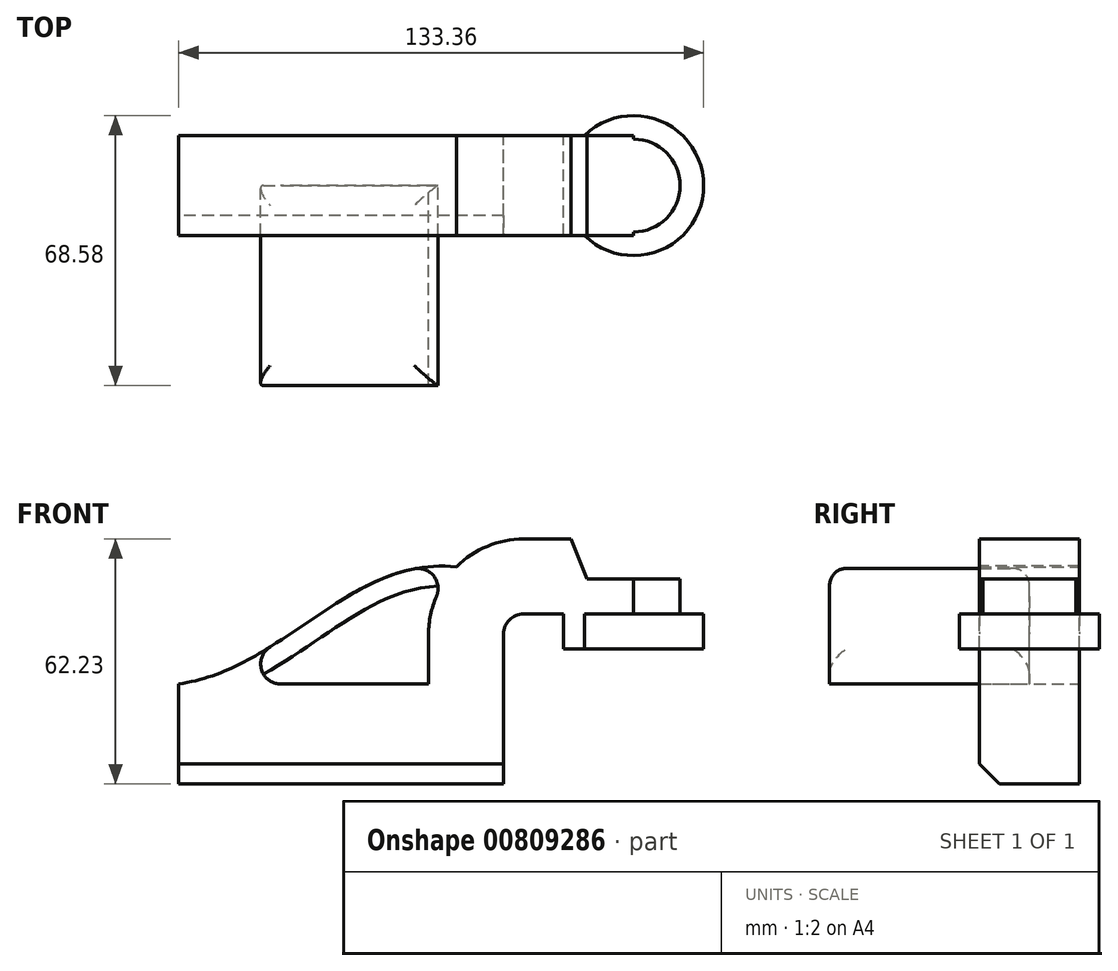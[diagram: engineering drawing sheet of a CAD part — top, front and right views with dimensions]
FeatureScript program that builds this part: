
annotation { "Feature Type Name" : "Feature", "Feature Type Description" : "" }
export const myFeature = defineFeature(function(context is Context, id is Id, definition is map)
    precondition{}
    {
        {
            var Q0;
            Q0=qCreatedBy(makeId("Front.planeOp"),FACE);
            var sketch = newSketch(context, id + "F0", { "sketchPlane" : qUnion([Q0])});
            skLineSegment(sketch, "E0.bottom", {"start": v(41.28, -12.7) * mm, "end": v(-41.28, -12.7) * mm});
            skLineSegment(sketch, "E0.top", {"start": v(41.28, 12.7) * mm, "end": v(-41.28, 12.7) * mm});
            skLineSegment(sketch, "E0.left", {"start": v(41.28, -12.7) * mm, "end": v(41.28, 12.7) * mm});
            skLineSegment(sketch, "E0.right", {"start": v(-41.28, -12.7) * mm, "end": v(-41.28, 12.7) * mm});
            skPoint(sketch, "E0.middle", {"position": v(0, 0) * mm});
            skLineSegment(sketch, "E1.bottom", {"start": v(74.3, 21.6) * mm, "end": v(56.52, 21.6) * mm});
            skLineSegment(sketch, "E1.top", {"start": v(74.3, 39.37) * mm, "end": v(56.52, 39.37) * mm});
            skLineSegment(sketch, "E1.left", {"start": v(74.3, 21.6) * mm, "end": v(74.3, 39.37) * mm});
            skLineSegment(sketch, "E1.right", {"start": v(56.52, 21.6) * mm, "end": v(56.52, 39.37) * mm});
            skPoint(sketch, "E1.middle", {"position": v(65.4, 30.48) * mm});
            skLineSegment(sketch, "E2", {"start": v(41.28, 12.7) * mm, "end": v(41.28, 25.4) * mm});
            skArc(sketch, "E3", {"start": v(41.27, 25.4) * mm, "mid": v(42.76, 29) * mm, "end": v(46.35, 30.48) * mm});
            skLineSegment(sketch, "E4", {"start": v(46.35, 30.48) * mm, "end": v(62.5, 30.48) * mm});
            skLineSegment(sketch, "E5.0", {"start": v(46.36, 49.53) * mm, "end": v(58.43, 49.53) * mm});
            skArc(sketch, "E5.1", {"start": v(22.23, 25.4) * mm, "mid": v(29.3, 42.46) * mm, "end": v(46.36, 49.53) * mm});
            skLineSegment(sketch, "E5.2", {"start": v(22.22, 12.7) * mm, "end": v(22.22, 25.4) * mm});
            skLineSegment(sketch, "E6", {"start": v(62.5, 30.48) * mm, "end": v(62.5, 39.37) * mm});
            skLineSegment(sketch, "E7", {"start": v(62.5, 39.37) * mm, "end": v(58.43, 49.53) * mm});
            skFitSpline(sketch, "E8", {"points": [v(-41.28, 12.7) * mm, v(29.3, 42.46) * mm], "startDerivative": vector(79.37, 10.78) * mm, "endDerivative": vector(80.37, -8.6) * mm});
            skSolve(sketch);
        }
        {
            var Q0;
            Q0 = qSketchRegion(id + "F0", true);
            extrude(context, id + "F1", {"entities" : qUnion([Q0]), "endBound" : BoundingType.SYMMETRIC, "depth" : 25.4 * mm, "offsetDistance" : 25.4 * mm});
        }
        {
            var Q0;
            {var subQ2=sQuery(id+"F0.wireOp",EDGE,"E5.2");Q0=makeQuery(id+"F0.imprint","IMPRINT",FACE,{"disambiguationData":[TD([[makeQuery(id+"F0.imprint","IMPRINT",EDGE,{"derivedFrom":subQ2}),1.0]])]});}
            extrude(context, id + "F2", {"entities" : qUnion([Q0]), "depth" : 50.8 * mm, "offsetDistance" : 25.4 * mm});
        }
        {
            var Q0;
            {var subQ1=sQuery(id+"F0.wireOp",EDGE,"E1.bottom");Q0=makeQuery(id+"F0.imprint","IMPRINT",FACE,{"disambiguationData":[TD([[makeQuery(id+"F0.imprint","IMPRINT",EDGE,{"derivedFrom":subQ1}),-1.0]])]});}
            var Q1;
            Q1=sQuery(id+"F0.wireOp",EDGE,"E1.left");
            revolve(context, id + "F3", {"operationType" : NewBodyOperationType.ADD, "surfaceOperationType" : NewSurfaceOperationType.NEW, "entities" : qUnion([Q0]), "axis" : qUnion([Q1]), "revolveType" : RevolveType.FULL});
        }
        {
            var Q0;
            Q0=makeQuery(id+"F2.opExtrude","SWEPT_FACE",FACE,{"disambiguationData":[OSD([sQuery(id+"F0.wireOp",EDGE,"E8")])]});
            fillet(context, id + "F4", {"entities" : qUnion([Q0]), "radius" : 5.08 * mm, "tangentPropagation" : true, "allowEdgeOverflow" : false});
        }
        {
            var Q0;
            Q0=makeQuery(id+"F1.opExtrude","CAP_EDGE",EDGE,{"disambiguationData":[OSD([sQuery(id+"F0.wireOp",EDGE,"E0.bottom")])],"isStart":false});
            chamfer(context, id + "F5", {"entities" : qUnion([Q0]), "width" : 5.08 * mm, "tangentPropagation" : true});
        }
    });
